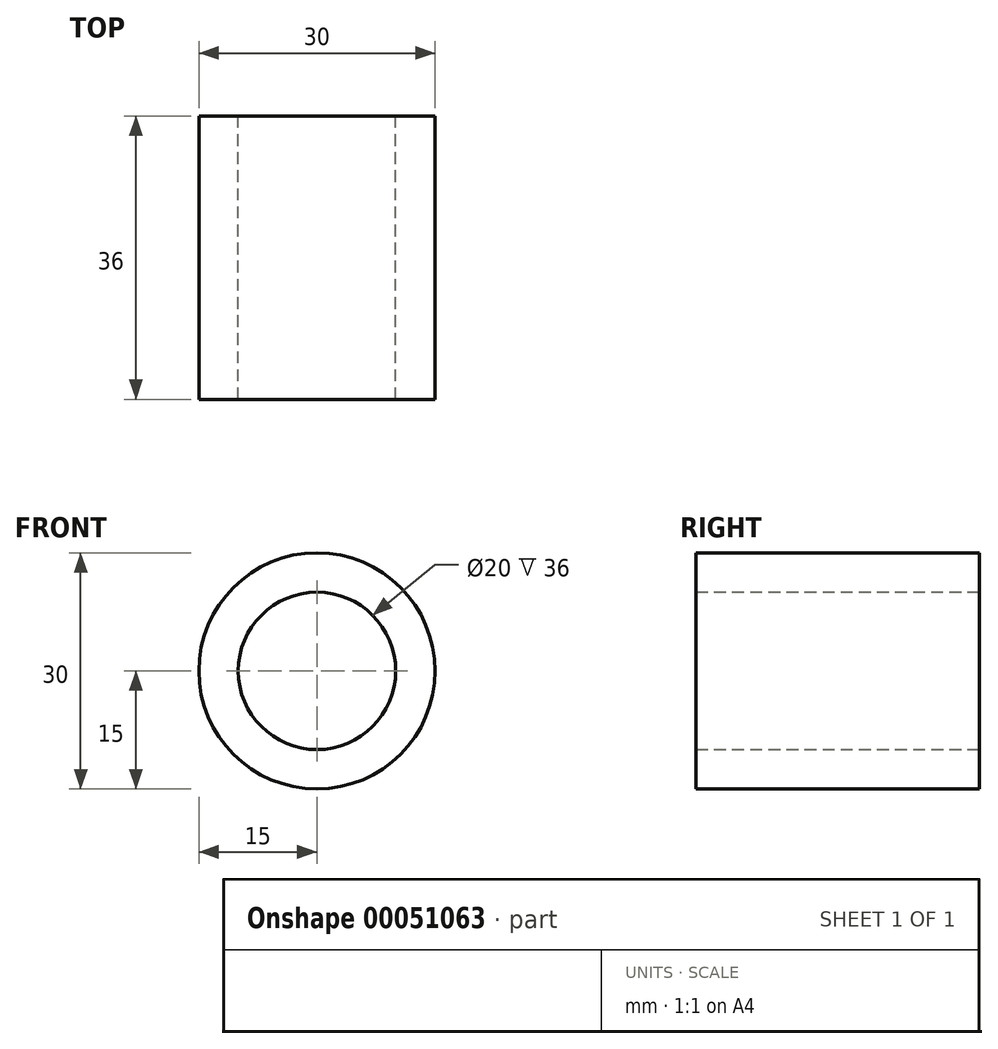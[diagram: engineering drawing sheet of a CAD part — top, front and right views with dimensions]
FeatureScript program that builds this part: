
annotation { "Feature Type Name" : "Feature", "Feature Type Description" : "" }
export const myFeature = defineFeature(function(context is Context, id is Id, definition is map)
    precondition{}
    {
        {
            var Q0;
            Q0=qCreatedBy(makeId("Front.planeOp"),FACE);
            var sketch = newSketch(context, id + "F0", { "sketchPlane" : qUnion([Q0])});
            skCircle(sketch, "E0", {"center": v(0, 0) * mm, "radius": 15 * mm});
            skCircle(sketch, "E1", {"center": v(0, 0) * mm, "radius": 10 * mm});
            skSolve(sketch);
        }
        {
            var Q0;
            Q0=makeQuery(id+"F0.imprint","IMPRINT",FACE,{"disambiguationData":[TD([[makeQuery(id+"F0.imprint","IMPRINT",EDGE,{"derivedFrom":sQuery(id+"F0.wireOp",EDGE,"E0")}),1.0]])]});
            extrude(context, id + "F1", {"entities" : qUnion([Q0]), "depth" : 36 * mm});
        }
    });
